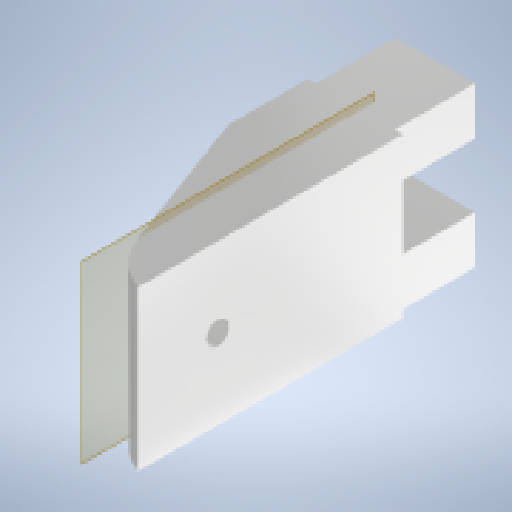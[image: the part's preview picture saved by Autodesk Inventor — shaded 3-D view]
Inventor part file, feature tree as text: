
AUTODESK INVENTOR PART (.ipt)
format: ipt  version: 2025 (Build 290162010, 162A)  size: 220,672 bytes
history: native  units: mm
features: sketch x6, other x4, extrude x3, hole x3, reference x2, plane x1
ambient origin geometry x8: Origin, YZ Plane, XZ Plane, XY Plane, X Axis, Y Axis, Z Axis, Center Point
bodies: Volumenkörper1 (feature_tree)
feature tree (19):
  extrude  "Extrusion1"  Depth=30.0mm TaperAngle=0.0deg
  hole  "Bohrung2"  [1 undecoded]
  sketch  "Skizze6"  dims[d16=1.567mm d17=8.0mm d18=4.0mm d19=2.0mm d20=90.0deg d21=10.0mm d22=20.594885mm d30=-8.0mm]
  plane  "Arbeitsebene1"
  hole  "Bohrung4"  [1 undecoded]
  extrude  "Extrusion2"  Depth=15.0mm
  hole  "Bohrung5"  [1 undecoded]
  extrude  "Extrusion3"  Depth=14.0mm
  sketch  "Skizze1"  dims[d0=5.0mm d1=45.0mm d2=30.0mm d3=0.0mm]
  reference  "Referenz1"
  sketch  "Skizze3"  dims[d4=15.0mm d14=6.5mm]
  reference  "Referenz3"
  sketch  "Skizze5"  dims[d15=5.0mm]
  sketch  "Skizze7"  dims[d31=15.0mm d32=15.0mm]
  sketch  "Skizze8"  dims[d33=3.2mm d34=6.0mm d35=6.3mm d36=2.0mm d37=90.0deg d38=8.0mm d39=20.594885mm d40=12.0mm d41=14.0mm d42=0.0mm d43=0.0mm d44=3.2mm d45=6.0mm d46=6.3mm d47=2.0mm d48=90.0deg d49=8.0mm d50=20.594885mm d51=12.0mm d52=8.0mm d53=0.0mm]
  other  "<userpath>\GIT\HDVKBM\CAD\Krandemonstrator\Demonstrator.iam"
  other  "Demonstrator.iam"
  other  "Träger:1"
  other  "AS 1112 (2) - Metrisch M4  Typ 5:1"
note: 3 required parameter values undecoded (feature->parameter linkage not recoverable at this tier; creation-order binding heuristic only, values carry confidence <= 0.55)
